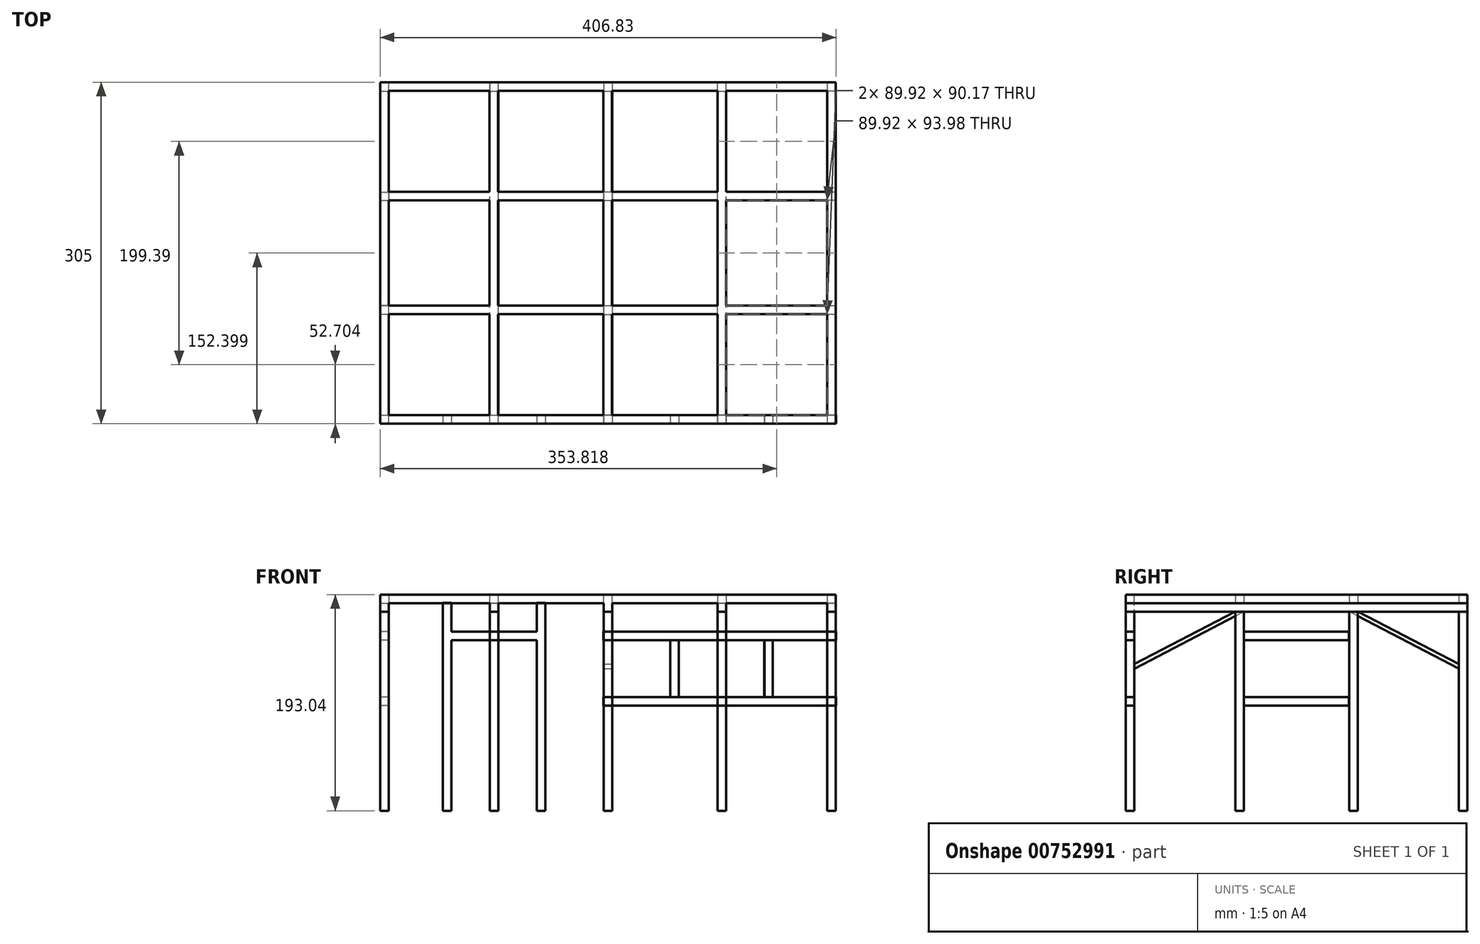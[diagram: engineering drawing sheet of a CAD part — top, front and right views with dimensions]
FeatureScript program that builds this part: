
annotation { "Feature Type Name" : "Feature", "Feature Type Description" : "" }
export const myFeature = defineFeature(function(context is Context, id is Id, definition is map)
    precondition{}
    {
        {
            var Q0;
            Q0=qCreatedBy(makeId("Top.planeOp"),FACE);
            var sketch = newSketch(context, id + "F0", { "sketchPlane" : qUnion([Q0])});
            skLineSegment(sketch, "E0.bottom", {"start": v(623.61, 433.43) * mm, "end": v(1030.01, 433.43) * mm});
            skLineSegment(sketch, "E0.top", {"start": v(623.61, 128.63) * mm, "end": v(1030.01, 128.63) * mm});
            skLineSegment(sketch, "E0.left", {"start": v(623.61, 433.43) * mm, "end": v(623.61, 128.63) * mm});
            skLineSegment(sketch, "E0.right", {"start": v(1030.01, 433.43) * mm, "end": v(1030.01, 128.63) * mm});
            skSolve(sketch);
        }
        {
            var Q0;
            Q0=makeQuery(id+"F0.imprint","IMPRINT",FACE,{"disambiguationData":[TD([[makeQuery(id+"F0.imprint","IMPRINT",EDGE,{"derivedFrom":sQuery(id+"F0.wireOp",EDGE,"E0.bottom")}),-1.0]])]});
            var sketch = newSketch(context, id + "F1", { "sketchPlane" : qUnion([Q0])});
            skLineSegment(sketch, "E1.bottom", {"start": v(623.7, 433.5) * mm, "end": v(631.33, 433.5) * mm});
            skLineSegment(sketch, "E1.top", {"start": v(623.7, 425.87) * mm, "end": v(631.33, 425.87) * mm});
            skLineSegment(sketch, "E1.left", {"start": v(623.7, 433.5) * mm, "end": v(623.7, 425.87) * mm});
            skLineSegment(sketch, "E1.right", {"start": v(631.33, 433.5) * mm, "end": v(631.33, 425.87) * mm});
            skLineSegment(sketch, "E2", {"start": v(1030.06, 433.5) * mm, "end": v(1022.44, 433.5) * mm, "construction": true});
            skLineSegment(sketch, "E3", {"start": v(1022.44, 433.5) * mm, "end": v(1022.44, 425.87) * mm, "construction": true});
            skLineSegment(sketch, "E4", {"start": v(1022.44, 425.87) * mm, "end": v(1030.06, 425.87) * mm, "construction": true});
            skLineSegment(sketch, "E5", {"start": v(1030.06, 425.87) * mm, "end": v(1030.06, 433.5) * mm, "construction": true});
            skLineSegment(sketch, "E6.bottom", {"start": v(623.58, 128.76) * mm, "end": v(631.33, 128.76) * mm});
            skLineSegment(sketch, "E6.top", {"start": v(623.58, 136.4) * mm, "end": v(631.33, 136.4) * mm});
            skLineSegment(sketch, "E6.left", {"start": v(623.58, 128.76) * mm, "end": v(623.58, 136.4) * mm});
            skLineSegment(sketch, "E6.right", {"start": v(631.33, 128.76) * mm, "end": v(631.33, 136.4) * mm});
            skLineSegment(sketch, "E7.bottom", {"start": v(1022.44, 136.4) * mm, "end": v(1030.06, 136.4) * mm});
            skLineSegment(sketch, "E7.top", {"start": v(1022.44, 128.76) * mm, "end": v(1030.06, 128.76) * mm});
            skLineSegment(sketch, "E7.left", {"start": v(1022.44, 136.4) * mm, "end": v(1022.44, 128.76) * mm});
            skLineSegment(sketch, "E7.right", {"start": v(1030.06, 136.4) * mm, "end": v(1030.06, 128.76) * mm});
            skLineSegment(sketch, "E8", {"start": v(623.7, 433.5) * mm, "end": v(823.1, 433.5) * mm});
            skLineSegment(sketch, "E9", {"start": v(623.7, 425.87) * mm, "end": v(721.5, 425.87) * mm});
            skLineSegment(sketch, "E10.bottom", {"start": v(721.5, 425.87) * mm, "end": v(729.12, 425.87) * mm});
            skLineSegment(sketch, "E10.top", {"start": v(721.5, 433.5) * mm, "end": v(729.12, 433.5) * mm});
            skLineSegment(sketch, "E10.left", {"start": v(721.5, 425.87) * mm, "end": v(721.5, 433.5) * mm});
            skLineSegment(sketch, "E10.right", {"start": v(729.12, 425.87) * mm, "end": v(729.12, 433.5) * mm});
            skLineSegment(sketch, "E11.bottom", {"start": v(823.1, 433.5) * mm, "end": v(830.72, 433.5) * mm});
            skLineSegment(sketch, "E11.top", {"start": v(823.1, 425.87) * mm, "end": v(830.72, 425.87) * mm});
            skLineSegment(sketch, "E11.left", {"start": v(823.1, 433.5) * mm, "end": v(823.1, 425.87) * mm});
            skLineSegment(sketch, "E11.right", {"start": v(830.72, 433.5) * mm, "end": v(830.72, 425.87) * mm});
            skLineSegment(sketch, "E12", {"start": v(623.7, 425.87) * mm, "end": v(924.7, 425.87) * mm});
            skLineSegment(sketch, "E13.bottom", {"start": v(924.7, 425.87) * mm, "end": v(932.32, 425.87) * mm});
            skLineSegment(sketch, "E13.top", {"start": v(924.7, 433.5) * mm, "end": v(932.32, 433.5) * mm});
            skLineSegment(sketch, "E13.left", {"start": v(924.7, 425.87) * mm, "end": v(924.7, 433.5) * mm});
            skLineSegment(sketch, "E13.right", {"start": v(932.32, 425.87) * mm, "end": v(932.32, 433.5) * mm});
            skLineSegment(sketch, "E14.bottom", {"start": v(729.12, 136.4) * mm, "end": v(721.5, 136.4) * mm});
            skLineSegment(sketch, "E14.top", {"start": v(729.12, 128.76) * mm, "end": v(721.5, 128.76) * mm});
            skLineSegment(sketch, "E14.left", {"start": v(729.12, 136.4) * mm, "end": v(729.12, 128.76) * mm});
            skLineSegment(sketch, "E14.right", {"start": v(721.5, 136.4) * mm, "end": v(721.5, 128.76) * mm});
            skLineSegment(sketch, "E15.bottom", {"start": v(830.72, 136.4) * mm, "end": v(823.1, 136.4) * mm});
            skLineSegment(sketch, "E15.top", {"start": v(830.72, 128.76) * mm, "end": v(823.1, 128.76) * mm});
            skLineSegment(sketch, "E15.left", {"start": v(830.72, 136.4) * mm, "end": v(830.72, 128.76) * mm});
            skLineSegment(sketch, "E15.right", {"start": v(823.1, 136.4) * mm, "end": v(823.1, 128.76) * mm});
            skLineSegment(sketch, "E16.bottom", {"start": v(924.7, 136.4) * mm, "end": v(932.32, 136.4) * mm});
            skLineSegment(sketch, "E16.top", {"start": v(924.7, 128.76) * mm, "end": v(932.32, 128.76) * mm});
            skLineSegment(sketch, "E16.left", {"start": v(924.7, 136.4) * mm, "end": v(924.7, 128.76) * mm});
            skLineSegment(sketch, "E16.right", {"start": v(932.32, 136.4) * mm, "end": v(932.32, 128.76) * mm});
            skLineSegment(sketch, "E17", {"start": v(623.7, 433.5) * mm, "end": v(623.7, 335.7) * mm});
            skLineSegment(sketch, "E18.bottom", {"start": v(623.7, 335.7) * mm, "end": v(631.33, 335.7) * mm});
            skLineSegment(sketch, "E18.top", {"start": v(623.7, 328.09) * mm, "end": v(631.33, 328.09) * mm});
            skLineSegment(sketch, "E18.left", {"start": v(623.7, 335.7) * mm, "end": v(623.7, 328.09) * mm});
            skLineSegment(sketch, "E18.right", {"start": v(631.33, 335.7) * mm, "end": v(631.33, 328.09) * mm});
            skLineSegment(sketch, "E19", {"start": v(623.58, 128.76) * mm, "end": v(623.58, 226.55) * mm});
            skLineSegment(sketch, "E20.bottom", {"start": v(623.58, 226.55) * mm, "end": v(631.33, 226.55) * mm});
            skLineSegment(sketch, "E20.top", {"start": v(623.58, 234.17) * mm, "end": v(631.33, 234.17) * mm});
            skLineSegment(sketch, "E20.left", {"start": v(623.58, 226.55) * mm, "end": v(623.58, 234.17) * mm});
            skLineSegment(sketch, "E20.right", {"start": v(631.33, 226.55) * mm, "end": v(631.33, 234.17) * mm});
            skLineSegment(sketch, "E21.bottom", {"start": v(1022.44, 226.55) * mm, "end": v(1030.06, 226.55) * mm});
            skLineSegment(sketch, "E21.top", {"start": v(1022.44, 234.17) * mm, "end": v(1030.06, 234.17) * mm});
            skLineSegment(sketch, "E21.left", {"start": v(1022.44, 226.55) * mm, "end": v(1022.44, 234.17) * mm});
            skLineSegment(sketch, "E21.right", {"start": v(1030.06, 226.55) * mm, "end": v(1030.06, 234.17) * mm});
            skLineSegment(sketch, "E22.bottom", {"start": v(1030.06, 328.09) * mm, "end": v(1022.44, 328.09) * mm});
            skLineSegment(sketch, "E22.top", {"start": v(1030.06, 335.7) * mm, "end": v(1022.44, 335.7) * mm});
            skLineSegment(sketch, "E22.left", {"start": v(1030.06, 328.09) * mm, "end": v(1030.06, 335.7) * mm});
            skLineSegment(sketch, "E22.right", {"start": v(1022.44, 328.09) * mm, "end": v(1022.44, 335.7) * mm});
            skLineSegment(sketch, "E23.bottom", {"start": v(1030.06, 433.5) * mm, "end": v(1022.44, 433.5) * mm});
            skLineSegment(sketch, "E23.top", {"start": v(1030.06, 425.87) * mm, "end": v(1022.44, 425.87) * mm});
            skLineSegment(sketch, "E23.left", {"start": v(1030.06, 433.5) * mm, "end": v(1030.06, 425.87) * mm});
            skLineSegment(sketch, "E23.right", {"start": v(1022.44, 433.5) * mm, "end": v(1022.44, 425.87) * mm});
            skSolve(sketch);
        }
        {
            var Q0;
            Q0 = qSketchRegion(id + "F1", true);
            extrude(context, id + "F2", {"entities" : qUnion([Q0]), "depth" : 177.8 * mm, "offsetDistance" : 25.4 * mm});
        }
        {
            var Q0;
            Q0=makeQuery(id+"F2.opExtrude","CAP_FACE",FACE,{"disambiguationData":[OSD([sQuery(id+"F1.wireOp",EDGE,"E8"),sQuery(id+"F1.wireOp",EDGE,"E10.top"),sQuery(id+"F1.wireOp",EDGE,"E11.bottom"),sQuery(id+"F1.wireOp",EDGE,"E11.right"),sQuery(id+"F1.wireOp",EDGE,"E12"),sQuery(id+"F1.wireOp",EDGE,"E17")])],"isStart":false});
            var sketch = newSketch(context, id + "F3", { "sketchPlane" : qUnion([Q0])});
            skLineSegment(sketch, "E24", {"start": v(623.7, 433.5) * mm, "end": v(631.33, 433.5) * mm});
            skLineSegment(sketch, "E25", {"start": v(631.33, 433.5) * mm, "end": v(721.5, 433.5) * mm});
            skLineSegment(sketch, "E26", {"start": v(721.5, 433.5) * mm, "end": v(721.5, 425.87) * mm});
            skPoint(sketch, "E26.endSnap0", {"position": v(727.21, 425.87) * mm});
            skLineSegment(sketch, "E27", {"start": v(721.5, 425.87) * mm, "end": v(631.33, 425.87) * mm});
            skLineSegment(sketch, "E28", {"start": v(631.33, 425.87) * mm, "end": v(631.33, 433.5) * mm});
            skLineSegment(sketch, "E29", {"start": v(721.5, 433.5) * mm, "end": v(729.12, 433.5) * mm});
            skLineSegment(sketch, "E30", {"start": v(830.72, 433.5) * mm, "end": v(823.1, 433.5) * mm});
            skLineSegment(sketch, "E31", {"start": v(823.1, 433.5) * mm, "end": v(729.12, 433.5) * mm});
            skLineSegment(sketch, "E32", {"start": v(823.1, 433.5) * mm, "end": v(823.1, 425.87) * mm});
            skLineSegment(sketch, "E33", {"start": v(823.1, 425.87) * mm, "end": v(729.12, 425.87) * mm});
            skLineSegment(sketch, "E34", {"start": v(729.12, 425.87) * mm, "end": v(729.12, 433.5) * mm});
            skSolve(sketch);
        }
        {
            var Q0;
            Q0 = qSketchRegion(id + "F3", true);
            extrude(context, id + "F4", {"entities" : qUnion([Q0]), "operationType" : NewBodyOperationType.REMOVE, "oppositeDirection" : true, "depth" : 177.8 * mm, "offsetDistance" : 25.4 * mm});
        }
        {
            var Q0;
            Q0=makeQuery(id+"F2.opExtrude","CAP_FACE",FACE,{"disambiguationData":[OSD([sQuery(id+"F1.wireOp",EDGE,"E6.bottom"),sQuery(id+"F1.wireOp",EDGE,"E6.top"),sQuery(id+"F1.wireOp",EDGE,"E6.right"),sQuery(id+"F1.wireOp",EDGE,"E19")])],"isStart":false});
            var sketch = newSketch(context, id + "F5", { "sketchPlane" : qUnion([Q0])});
            skLineSegment(sketch, "E35.bottom", {"start": v(623.58, 128.76) * mm, "end": v(631.33, 128.76) * mm});
            skLineSegment(sketch, "E35.top", {"start": v(623.58, 433.6) * mm, "end": v(631.33, 433.6) * mm});
            skLineSegment(sketch, "E35.left", {"start": v(623.58, 128.76) * mm, "end": v(623.58, 433.6) * mm});
            skLineSegment(sketch, "E35.right", {"start": v(631.33, 128.76) * mm, "end": v(631.33, 433.6) * mm});
            skLineSegment(sketch, "E36.bottom", {"start": v(729.24, 128.76) * mm, "end": v(721.53, 128.76) * mm});
            skLineSegment(sketch, "E36.top", {"start": v(729.24, 433.6) * mm, "end": v(721.53, 433.6) * mm});
            skLineSegment(sketch, "E36.left", {"start": v(729.24, 128.76) * mm, "end": v(729.24, 433.6) * mm});
            skLineSegment(sketch, "E36.right", {"start": v(721.53, 128.76) * mm, "end": v(721.53, 433.6) * mm});
            skLineSegment(sketch, "E37.bottom", {"start": v(830.67, 433.6) * mm, "end": v(823.1, 433.6) * mm});
            skLineSegment(sketch, "E37.top", {"start": v(830.67, 128.76) * mm, "end": v(823.1, 128.76) * mm});
            skLineSegment(sketch, "E37.left", {"start": v(830.67, 433.6) * mm, "end": v(830.67, 128.76) * mm});
            skLineSegment(sketch, "E37.right", {"start": v(823.1, 433.6) * mm, "end": v(823.1, 128.76) * mm});
            skLineSegment(sketch, "E38.bottom", {"start": v(932.35, 128.76) * mm, "end": v(924.7, 128.76) * mm});
            skLineSegment(sketch, "E38.top", {"start": v(932.35, 433.6) * mm, "end": v(924.7, 433.6) * mm});
            skLineSegment(sketch, "E38.left", {"start": v(932.35, 128.76) * mm, "end": v(932.35, 433.6) * mm});
            skLineSegment(sketch, "E38.right", {"start": v(924.7, 128.76) * mm, "end": v(924.7, 433.6) * mm});
            skLineSegment(sketch, "E39.bottom", {"start": v(1030.15, 433.6) * mm, "end": v(1022.43, 433.6) * mm});
            skLineSegment(sketch, "E39.top", {"start": v(1030.15, 128.76) * mm, "end": v(1022.43, 128.76) * mm});
            skLineSegment(sketch, "E39.left", {"start": v(1030.15, 433.6) * mm, "end": v(1030.15, 128.76) * mm});
            skLineSegment(sketch, "E39.right", {"start": v(1022.43, 433.6) * mm, "end": v(1022.43, 128.76) * mm});
            skSolve(sketch);
        }
        {
            var Q0;
            Q0 = qSketchRegion(id + "F5", true);
            extrude(context, id + "F6", {"entities" : qUnion([Q0]), "depth" : 7.62 * mm, "offsetDistance" : 25.4 * mm});
        }
        {
            var Q0;
            Q0=makeQuery(id+"F6.opExtrude","CAP_FACE",FACE,{"disambiguationData":[OSD([sQuery(id+"F5.wireOp",EDGE,"E35.bottom"),sQuery(id+"F5.wireOp",EDGE,"E35.top"),sQuery(id+"F5.wireOp",EDGE,"E35.left"),sQuery(id+"F5.wireOp",EDGE,"E35.right")])],"isStart":false});
            var sketch = newSketch(context, id + "F7", { "sketchPlane" : qUnion([Q0])});
            skLineSegment(sketch, "E40.bottom", {"start": v(623.58, 128.76) * mm, "end": v(1029.98, 128.76) * mm});
            skLineSegment(sketch, "E40.top", {"start": v(623.58, 136.38) * mm, "end": v(1029.98, 136.38) * mm});
            skLineSegment(sketch, "E40.left", {"start": v(623.58, 128.76) * mm, "end": v(623.58, 136.38) * mm});
            skLineSegment(sketch, "E40.right", {"start": v(1029.98, 128.76) * mm, "end": v(1029.98, 136.38) * mm});
            skLineSegment(sketch, "E41", {"start": v(623.58, 128.76) * mm, "end": v(623.58, 226.55) * mm});
            skLineSegment(sketch, "E42", {"start": v(623.58, 128.76) * mm, "end": v(623.58, 328.15) * mm});
            skLineSegment(sketch, "E43", {"start": v(623.58, 128.76) * mm, "end": v(623.58, 425.94) * mm});
            skLineSegment(sketch, "E44.bottom", {"start": v(623.58, 226.55) * mm, "end": v(1029.98, 226.55) * mm});
            skLineSegment(sketch, "E44.top", {"start": v(623.58, 234.17) * mm, "end": v(1029.98, 234.17) * mm});
            skLineSegment(sketch, "E44.left", {"start": v(623.58, 226.55) * mm, "end": v(623.58, 234.17) * mm});
            skLineSegment(sketch, "E44.right", {"start": v(1029.98, 226.55) * mm, "end": v(1029.98, 234.17) * mm});
            skLineSegment(sketch, "E45.bottom", {"start": v(623.58, 328.15) * mm, "end": v(1029.98, 328.15) * mm});
            skLineSegment(sketch, "E45.top", {"start": v(623.58, 335.77) * mm, "end": v(1029.98, 335.77) * mm});
            skLineSegment(sketch, "E45.left", {"start": v(623.58, 328.15) * mm, "end": v(623.58, 335.77) * mm});
            skLineSegment(sketch, "E45.right", {"start": v(1029.98, 328.15) * mm, "end": v(1029.98, 335.77) * mm});
            skLineSegment(sketch, "E46.bottom", {"start": v(623.58, 425.94) * mm, "end": v(1029.98, 425.94) * mm});
            skLineSegment(sketch, "E46.top", {"start": v(623.58, 433.6) * mm, "end": v(1029.98, 433.6) * mm});
            skLineSegment(sketch, "E46.left", {"start": v(623.58, 425.94) * mm, "end": v(623.58, 433.6) * mm});
            skLineSegment(sketch, "E46.right", {"start": v(1029.98, 425.94) * mm, "end": v(1029.98, 433.6) * mm});
            skSolve(sketch);
        }
        {
            var Q0;
            Q0 = qSketchRegion(id + "F7", true);
            extrude(context, id + "F8", {"entities" : qUnion([Q0]), "depth" : 7.62 * mm, "offsetDistance" : 25.4 * mm});
        }
        {
            var Q0;
            Q0=makeQuery(id+"F2.opExtrude","SWEPT_FACE",FACE,{"disambiguationData":[OSD([sQuery(id+"F1.wireOp",EDGE,"E11.right")])]});
            var sketch = newSketch(context, id + "F9", { "sketchPlane" : qUnion([Q0])});
            skLineSegment(sketch, "E47", {"start": v(425.87, 0) * mm, "end": v(425.87, 127) * mm});
            skLineSegment(sketch, "E48", {"start": v(425.87, 127) * mm, "end": v(328.29, 177.8) * mm});
            skLineSegment(sketch, "E49", {"start": v(328.29, 177.8) * mm, "end": v(336.01, 177.8) * mm});
            skLineSegment(sketch, "E50", {"start": v(336.01, 177.8) * mm, "end": v(425.87, 131.02) * mm});
            skLineSegment(sketch, "E51", {"start": v(425.87, 131.02) * mm, "end": v(425.87, 127) * mm});
            skLineSegment(sketch, "E52", {"start": v(136.65, 127) * mm, "end": v(234.28, 177.8) * mm});
            skLineSegment(sketch, "E53", {"start": v(234.28, 177.8) * mm, "end": v(226.35, 177.8) * mm});
            skLineSegment(sketch, "E54", {"start": v(226.35, 177.8) * mm, "end": v(136.45, 131.02) * mm});
            skLineSegment(sketch, "E55", {"start": v(136.45, 131.02) * mm, "end": v(136.65, 127) * mm});
            skSolve(sketch);
        }
        {
            var Q0;
            Q0 = qSketchRegion(id + "F9", true);
            extrude(context, id + "F10", {"entities" : qUnion([Q0]), "oppositeDirection" : true, "depth" : 7.62 * mm, "offsetDistance" : 25.4 * mm});
        }
        {
            var Q0;
            Q0=makeQuery(id+"F2.opExtrude","SWEPT_FACE",FACE,{"disambiguationData":[OSD([sQuery(id+"F1.wireOp",EDGE,"E7.top")])]});
            var sketch = newSketch(context, id + "F11", { "sketchPlane" : qUnion([Q0])});
            skLineSegment(sketch, "E56", {"start": v(623.82, 0) * mm, "end": v(890.52, 0) * mm});
            skLineSegment(sketch, "E57", {"start": v(890.52, 0) * mm, "end": v(966.72, 0) * mm});
            skLineSegment(sketch, "E58", {"start": v(966.72, 101.6) * mm, "end": v(966.72, 0) * mm});
            skLineSegment(sketch, "E59", {"start": v(966.72, 101.6) * mm, "end": v(966.72, 152.4) * mm});
            skLineSegment(sketch, "E60.bottom", {"start": v(966.72, 101.6) * mm, "end": v(890.52, 101.6) * mm});
            skLineSegment(sketch, "E60.top", {"start": v(966.72, 152.4) * mm, "end": v(890.52, 152.4) * mm});
            skLineSegment(sketch, "E60.right", {"start": v(890.52, 101.6) * mm, "end": v(890.52, 152.4) * mm});
            skSolve(sketch);
        }
        {
            var Q0;
            Q0 = qSketchRegion(id + "F11", true);
            extrude(context, id + "F12", {"entities" : qUnion([Q0]), "operationType" : NewBodyOperationType.REMOVE, "oppositeDirection" : true, "depth" : 10.16 * mm, "offsetDistance" : 25.4 * mm});
        }
        {
            var Q0;
            {var subQ2=sQuery(id+"F1.wireOp",EDGE,"E16.top");Q0=makeQuery(id+"F12.boolean.opBoolean","SPLIT",FACE,{"disambiguationData":[TD([makeQuery(id+"F12.opExtrude","SWEPT_FACE",FACE,{"disambiguationData":[OSD([sQuery(id+"F11.wireOp",EDGE,"E60.top")])]})])],"derivedFrom":makeQuery(id+"F2.opExtrude","SWEPT_FACE",FACE,{"disambiguationData":[OSD([subQ2])]})});}
            var sketch = newSketch(context, id + "F13", { "sketchPlane" : qUnion([Q0])});
            skLineSegment(sketch, "E61.bottom", {"start": v(1030.41, 152.4) * mm, "end": v(822.92, 152.4) * mm});
            skLineSegment(sketch, "E61.top", {"start": v(1030.41, 160.02) * mm, "end": v(822.92, 160.02) * mm});
            skLineSegment(sketch, "E61.left", {"start": v(1030.41, 152.4) * mm, "end": v(1030.41, 160.02) * mm});
            skLineSegment(sketch, "E61.right", {"start": v(822.92, 152.4) * mm, "end": v(822.92, 160.02) * mm});
            skLineSegment(sketch, "E62", {"start": v(932.32, 0) * mm, "end": v(932.32, 93.98) * mm});
            skLineSegment(sketch, "E63.bottom", {"start": v(1030.41, 93.98) * mm, "end": v(822.92, 93.98) * mm});
            skLineSegment(sketch, "E63.top", {"start": v(1030.41, 101.6) * mm, "end": v(822.92, 101.6) * mm});
            skLineSegment(sketch, "E63.left", {"start": v(1030.41, 93.98) * mm, "end": v(1030.41, 101.6) * mm});
            skLineSegment(sketch, "E63.right", {"start": v(822.92, 93.98) * mm, "end": v(822.92, 101.6) * mm});
            skSolve(sketch);
        }
        {
            var Q0;
            Q0 = qSketchRegion(id + "F13", true);
            extrude(context, id + "F14", {"entities" : qUnion([Q0]), "oppositeDirection" : true, "depth" : 7.62 * mm, "offsetDistance" : 25.4 * mm});
        }
        {
            var Q0;
            Q0=makeQuery(id+"F14.opExtrude","CAP_FACE",FACE,{"disambiguationData":[OSD([sQuery(id+"F13.wireOp",EDGE,"E63.bottom"),sQuery(id+"F13.wireOp",EDGE,"E63.top"),sQuery(id+"F13.wireOp",EDGE,"E63.left"),sQuery(id+"F13.wireOp",EDGE,"E63.right")])],"isStart":true});
            var sketch = newSketch(context, id + "F15", { "sketchPlane" : qUnion([Q0])});
            skLineSegment(sketch, "E64", {"start": v(822.92, 93.98) * mm, "end": v(890.23, 93.98) * mm});
            skLineSegment(sketch, "E65", {"start": v(890.23, 93.98) * mm, "end": v(966.43, 93.98) * mm});
            skLineSegment(sketch, "E66", {"start": v(974.05, 101.6) * mm, "end": v(966.43, 101.6) * mm});
            skLineSegment(sketch, "E67", {"start": v(974.05, 101.6) * mm, "end": v(974.05, 152.4) * mm});
            skLineSegment(sketch, "E68", {"start": v(974.05, 152.4) * mm, "end": v(966.43, 152.4) * mm});
            skLineSegment(sketch, "E69", {"start": v(966.43, 101.6) * mm, "end": v(966.43, 152.4) * mm});
            skLineSegment(sketch, "E70", {"start": v(822.92, 93.98) * mm, "end": v(878.2, 93.98) * mm});
            skLineSegment(sketch, "E71", {"start": v(822.92, 93.98) * mm, "end": v(882.61, 93.98) * mm});
            skLineSegment(sketch, "E72.bottom", {"start": v(890.23, 101.6) * mm, "end": v(882.61, 101.6) * mm});
            skLineSegment(sketch, "E72.top", {"start": v(890.23, 152.4) * mm, "end": v(882.61, 152.4) * mm});
            skLineSegment(sketch, "E72.left", {"start": v(890.23, 101.6) * mm, "end": v(890.23, 152.4) * mm});
            skLineSegment(sketch, "E72.right", {"start": v(882.61, 101.6) * mm, "end": v(882.61, 152.4) * mm});
            skSolve(sketch);
        }
        {
            var Q0;
            Q0 = qSketchRegion(id + "F15", true);
            extrude(context, id + "F16", {"entities" : qUnion([Q0]), "oppositeDirection" : true, "depth" : 7.62 * mm, "offsetDistance" : 25.4 * mm});
        }
        {
            var Q0;
            Q0=makeQuery(id+"F2.opExtrude","SWEPT_FACE",FACE,{"disambiguationData":[OSD([sQuery(id+"F1.wireOp",EDGE,"E20.left")])]});
            var sketch = newSketch(context, id + "F17", { "sketchPlane" : qUnion([Q0])});
            skLineSegment(sketch, "E73", {"start": v(-234.17, 0) * mm, "end": v(-234.17, 109.01) * mm});
            skLineSegment(sketch, "E74", {"start": v(-234.17, 0) * mm, "end": v(-234.17, 93.98) * mm});
            skLineSegment(sketch, "E75", {"start": v(-234.17, 93.98) * mm, "end": v(-234.17, 0) * mm});
            skLineSegment(sketch, "E76", {"start": v(-234.17, 0) * mm, "end": v(-234.17, 101.6) * mm});
            skLineSegment(sketch, "E77", {"start": v(-234.17, 101.6) * mm, "end": v(-327.8, 101.6) * mm});
            skLineSegment(sketch, "E78", {"start": v(-326.1, 93.98) * mm, "end": v(-234.17, 93.98) * mm});
            skLineSegment(sketch, "E79", {"start": v(-234.17, 101.6) * mm, "end": v(-234.17, 152.4) * mm});
            skLineSegment(sketch, "E80", {"start": v(-234.17, 160.02) * mm, "end": v(-234.17, 152.4) * mm});
            skLineSegment(sketch, "E81", {"start": v(-234.17, 160.02) * mm, "end": v(-327.8, 160.02) * mm});
            skLineSegment(sketch, "E82", {"start": v(-327.8, 160.02) * mm, "end": v(-327.8, 152.4) * mm});
            skLineSegment(sketch, "E83", {"start": v(-327.8, 152.4) * mm, "end": v(-234.17, 152.4) * mm});
            skLineSegment(sketch, "E84", {"start": v(-326.1, 93.98) * mm, "end": v(-327.8, 93.98) * mm});
            skLineSegment(sketch, "E85", {"start": v(-327.8, 101.6) * mm, "end": v(-327.8, 93.98) * mm});
            skSolve(sketch);
        }
        {
            var Q0;
            Q0 = qSketchRegion(id + "F17", true);
            extrude(context, id + "F18", {"entities" : qUnion([Q0]), "oppositeDirection" : true, "depth" : 7.62 * mm, "offsetDistance" : 25.4 * mm});
        }
        {
            var Q0;
            Q0=makeQuery(id+"F2.opExtrude","SWEPT_FACE",FACE,{"disambiguationData":[OSD([sQuery(id+"F1.wireOp",EDGE,"E14.top")])]});
            var sketch = newSketch(context, id + "F19", { "sketchPlane" : qUnion([Q0])});
            skLineSegment(sketch, "E86", {"start": v(725.3, 0) * mm, "end": v(725.3, 85.39) * mm});
            skLineSegment(sketch, "E87.bottom", {"start": v(687.2, 0) * mm, "end": v(763.4, 0) * mm});
            skLineSegment(sketch, "E87.top", {"start": v(687.2, 0) * mm, "end": v(763.4, 0) * mm});
            skLineSegment(sketch, "E87.left", {"start": v(687.2, 0) * mm, "end": v(687.2, 0) * mm});
            skLineSegment(sketch, "E87.right", {"start": v(763.4, 0) * mm, "end": v(763.4, 0) * mm});
            skPoint(sketch, "E87.middle", {"position": v(725.3, 0) * mm});
            skLineSegment(sketch, "E88", {"start": v(763.4, 0) * mm, "end": v(771.03, 0) * mm});
            skLineSegment(sketch, "E89", {"start": v(687.2, 0) * mm, "end": v(679.6, 0) * mm});
            skLineSegment(sketch, "E90.top", {"start": v(687.2, 185.64) * mm, "end": v(679.6, 185.64) * mm});
            skLineSegment(sketch, "E90.left", {"start": v(687.2, 0) * mm, "end": v(687.2, 185.64) * mm});
            skLineSegment(sketch, "E90.right", {"start": v(679.6, 0) * mm, "end": v(679.6, 185.64) * mm});
            skLineSegment(sketch, "E91.bottom", {"start": v(771.03, 0) * mm, "end": v(763.4, 0) * mm});
            skLineSegment(sketch, "E91.top", {"start": v(771.03, 185.64) * mm, "end": v(763.4, 185.64) * mm});
            skLineSegment(sketch, "E91.left", {"start": v(771.03, 0) * mm, "end": v(771.03, 185.64) * mm});
            skLineSegment(sketch, "E91.right", {"start": v(763.4, 0) * mm, "end": v(763.4, 185.64) * mm});
            skLineSegment(sketch, "E92", {"start": v(763.4, 0) * mm, "end": v(763.4, 152.4) * mm});
            skLineSegment(sketch, "E93", {"start": v(763.4, 152.4) * mm, "end": v(687.2, 152.4) * mm});
            skLineSegment(sketch, "E94", {"start": v(687.2, 160.02) * mm, "end": v(687.2, 152.4) * mm});
            skLineSegment(sketch, "E95", {"start": v(687.2, 160.02) * mm, "end": v(763.4, 160.02) * mm});
            skLineSegment(sketch, "E96", {"start": v(763.4, 160.02) * mm, "end": v(763.4, 152.4) * mm});
            skSolve(sketch);
        }
        {
            var Q0;
            Q0 = qSketchRegion(id + "F19", true);
            extrude(context, id + "F20", {"entities" : qUnion([Q0]), "oppositeDirection" : true, "depth" : 7.62 * mm, "offsetDistance" : 25.4 * mm});
        }
        {
            var Q0;
            Q0=makeQuery(id+"F20.opExtrude","CAP_FACE",FACE,{"disambiguationData":[OSD([sQuery(id+"F19.wireOp",EDGE,"E87.top"),sQuery(id+"F19.wireOp",EDGE,"E89"),sQuery(id+"F19.wireOp",EDGE,"E90.top"),sQuery(id+"F19.wireOp",EDGE,"E90.left"),sQuery(id+"F19.wireOp",EDGE,"E90.right"),sQuery(id+"F19.wireOp",EDGE,"E91.bottom"),sQuery(id+"F19.wireOp",EDGE,"E91.top"),sQuery(id+"F19.wireOp",EDGE,"E91.left"),sQuery(id+"F19.wireOp",EDGE,"E91.right"),sQuery(id+"F19.wireOp",EDGE,"E95")])],"isStart":true});
            var sketch = newSketch(context, id + "F21", { "sketchPlane" : qUnion([Q0])});
            skLineSegment(sketch, "E97", {"start": v(679.6, 0) * mm, "end": v(687.21, 0) * mm});
            skLineSegment(sketch, "E98", {"start": v(687.21, 0) * mm, "end": v(687.21, 152.4) * mm});
            skLineSegment(sketch, "E99", {"start": v(687.21, 152.4) * mm, "end": v(763.4, 152.4) * mm});
            skLineSegment(sketch, "E100", {"start": v(763.4, 152.4) * mm, "end": v(763.4, 0) * mm});
            skLineSegment(sketch, "E101", {"start": v(763.4, 0) * mm, "end": v(687.21, 0) * mm});
            skSolve(sketch);
        }
        {
            var Q0;
            Q0 = qSketchRegion(id + "F21", true);
            extrude(context, id + "F22", {"entities" : qUnion([Q0]), "operationType" : NewBodyOperationType.REMOVE, "oppositeDirection" : true, "depth" : 8.13 * mm, "offsetDistance" : 25.4 * mm});
        }
        {
            var Q0;
            Q0=makeQuery(id+"F8.opExtrude","CAP_FACE",FACE,{"disambiguationData":[OSD([sQuery(id+"F7.wireOp",EDGE,"E40.bottom"),sQuery(id+"F7.wireOp",EDGE,"E40.top"),sQuery(id+"F7.wireOp",EDGE,"E40.right"),sQuery(id+"F7.wireOp",EDGE,"E43")])],"isStart":false});
            var sketch = newSketch(context, id + "F23", { "sketchPlane" : qUnion([Q0])});
            skLineSegment(sketch, "E102.bottom", {"start": v(623.58, 128.76) * mm, "end": v(631.2, 128.76) * mm});
            skLineSegment(sketch, "E102.top", {"start": v(623.58, 433.76) * mm, "end": v(631.2, 433.76) * mm});
            skLineSegment(sketch, "E102.left", {"start": v(623.58, 128.76) * mm, "end": v(623.58, 433.76) * mm});
            skLineSegment(sketch, "E102.right", {"start": v(631.2, 128.76) * mm, "end": v(631.2, 433.76) * mm});
            skLineSegment(sketch, "E103.bottom", {"start": v(721.28, 136.38) * mm, "end": v(728.9, 136.38) * mm});
            skLineSegment(sketch, "E103.top", {"start": v(721.28, 433.76) * mm, "end": v(728.9, 433.76) * mm});
            skLineSegment(sketch, "E103.left", {"start": v(721.28, 136.38) * mm, "end": v(721.28, 433.76) * mm});
            skLineSegment(sketch, "E103.right", {"start": v(728.9, 136.38) * mm, "end": v(728.9, 433.76) * mm});
            skLineSegment(sketch, "E104.bottom", {"start": v(822.89, 136.38) * mm, "end": v(830.5, 136.38) * mm});
            skLineSegment(sketch, "E104.top", {"start": v(822.89, 426.72) * mm, "end": v(830.5, 426.72) * mm});
            skLineSegment(sketch, "E104.left", {"start": v(822.89, 136.38) * mm, "end": v(822.89, 426.72) * mm});
            skLineSegment(sketch, "E104.right", {"start": v(830.5, 136.38) * mm, "end": v(830.5, 426.72) * mm});
            skLineSegment(sketch, "E105.bottom", {"start": v(924.82, 136.38) * mm, "end": v(932.44, 136.38) * mm});
            skLineSegment(sketch, "E105.top", {"start": v(924.82, 433.76) * mm, "end": v(932.44, 433.76) * mm});
            skLineSegment(sketch, "E105.left", {"start": v(924.82, 136.38) * mm, "end": v(924.82, 433.76) * mm});
            skLineSegment(sketch, "E105.right", {"start": v(932.44, 136.38) * mm, "end": v(932.44, 433.76) * mm});
            skLineSegment(sketch, "E106.bottom", {"start": v(1022.36, 136.38) * mm, "end": v(1029.98, 136.38) * mm});
            skLineSegment(sketch, "E106.top", {"start": v(1022.36, 433.76) * mm, "end": v(1029.98, 433.76) * mm});
            skLineSegment(sketch, "E106.left", {"start": v(1022.36, 136.38) * mm, "end": v(1022.36, 433.76) * mm});
            skLineSegment(sketch, "E106.right", {"start": v(1029.98, 136.38) * mm, "end": v(1029.98, 433.76) * mm});
            skSolve(sketch);
        }
        {
            var Q0;
            Q0 = qSketchRegion(id + "F23", true);
            extrude(context, id + "F24", {"entities" : qUnion([Q0]), "operationType" : NewBodyOperationType.ADD, "oppositeDirection" : true, "depth" : 7.62 * mm, "offsetDistance" : 25.4 * mm});
        }
    });
